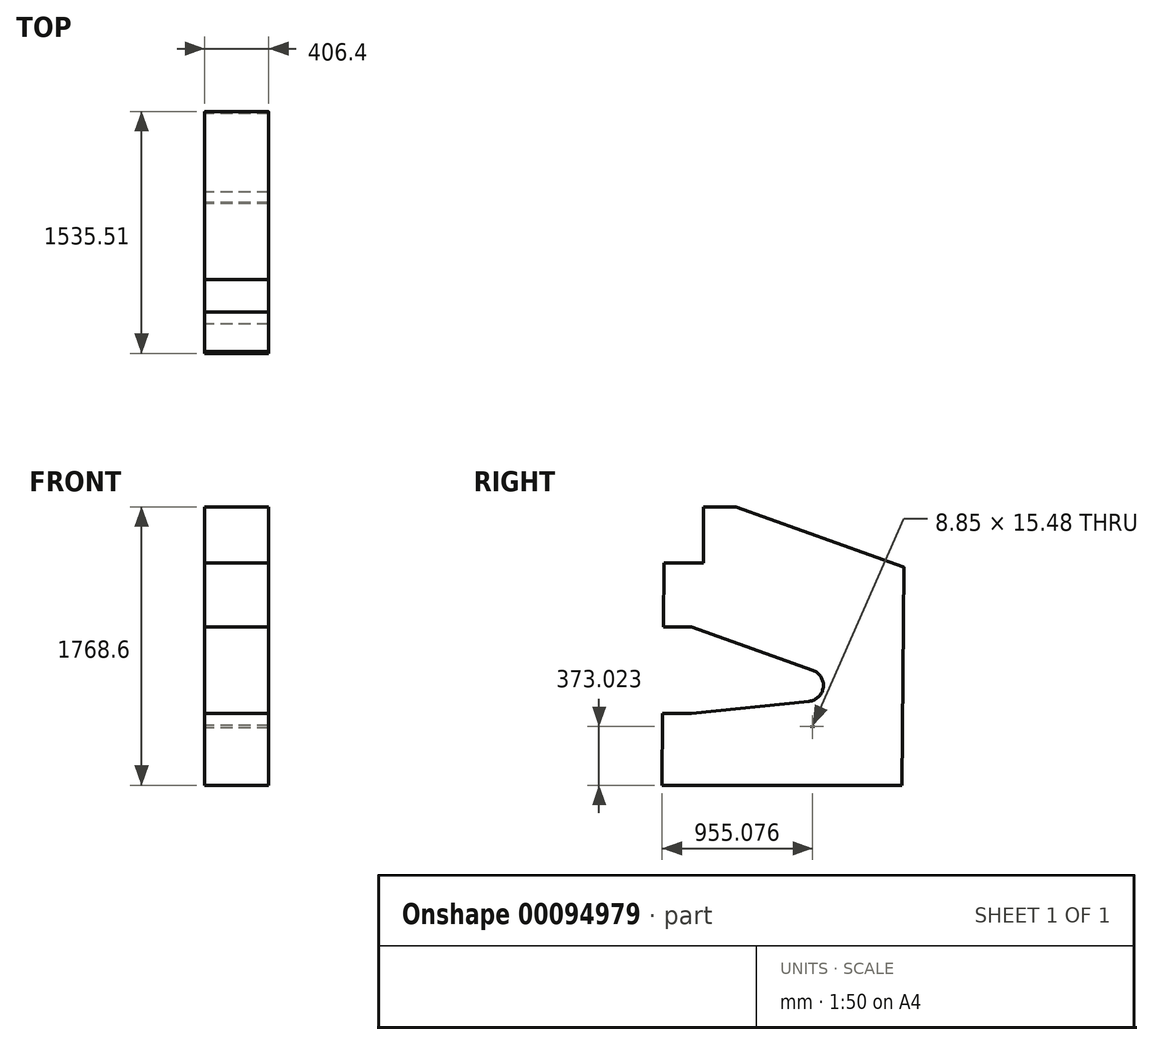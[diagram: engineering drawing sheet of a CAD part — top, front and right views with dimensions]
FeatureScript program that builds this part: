
annotation { "Feature Type Name" : "Feature", "Feature Type Description" : "" }
export const myFeature = defineFeature(function(context is Context, id is Id, definition is map)
    precondition{}
    {
        {
            var Q0;
            Q0=qCreatedBy(makeId("Right.planeOp"),FACE);
            var sketch = newSketch(context, id + "F0", { "sketchPlane" : qUnion([Q0])});
            skLineSegment(sketch, "E0.bottom", {"start": v(601.31, 0) * mm, "end": v(-922.74, 0) * mm});
            skLineSegment(sketch, "E0.top", {"start": v(-736.6, 457.2) * mm, "end": v(-918.95, 457.2) * mm});
            skLineSegment(sketch, "E0.right", {"start": v(-922.74, 0) * mm, "end": v(-918.95, 457.2) * mm});
            skLineSegment(sketch, "E1.bottom", {"start": v(27.91, 365.28) * mm, "end": v(36.76, 365.28) * mm});
            skLineSegment(sketch, "E1.top", {"start": v(27.91, 380.76) * mm, "end": v(36.76, 380.76) * mm});
            skLineSegment(sketch, "E1.left", {"start": v(27.91, 365.28) * mm, "end": v(27.91, 380.76) * mm});
            skLineSegment(sketch, "E1.right", {"start": v(36.76, 365.28) * mm, "end": v(36.76, 380.76) * mm});
            skLineSegment(sketch, "E2.0", {"start": v(-736.6, 1006.6) * mm, "end": v(-914.4, 1006.6) * mm});
            skLineSegment(sketch, "E3.0", {"start": v(-453.6, 1768.6) * mm, "end": v(-660.4, 1768.6) * mm});
            skLineSegment(sketch, "E4.0", {"start": v(0, 635) * mm, "end": v(-914.4, 635) * mm, "construction": true});
            skArc(sketch, "E5", {"start": v(10.38, 533.93) * mm, "mid": v(100.86, 622.77) * mm, "end": v(34.24, 730.66) * mm});
            skLineSegment(sketch, "E6", {"start": v(-736.6, 1221.83) * mm, "end": v(-736.6, 326.78) * mm, "construction": true});
            skLineSegment(sketch, "E7", {"start": v(-736.6, 1006.6) * mm, "end": v(34.24, 730.66) * mm});
            skLineSegment(sketch, "E8", {"start": v(-736.6, 457.2) * mm, "end": v(10.38, 533.93) * mm});
            skLineSegment(sketch, "E9.0", {"start": v(601.31, 0) * mm, "end": v(612.77, 1382.34) * mm});
            skLineSegment(sketch, "E10.0", {"start": v(-453.6, 1768.6) * mm, "end": v(608.56, 1388.37) * mm});
            skLineSegment(sketch, "E11", {"start": v(-911.03, 1413) * mm, "end": v(-660.4, 1413) * mm});
            skLineSegment(sketch, "E12", {"start": v(-660.4, 1413) * mm, "end": v(-660.4, 1768.6) * mm});
            skLineSegment(sketch, "E13", {"start": v(-914.4, 1006.6) * mm, "end": v(-911.03, 1413) * mm});
            skPoint(sketch, "E14.orphan", {"position": v(-909.8, 1413) * mm});
            skPoint(sketch, "E15.orphan", {"position": v(-909.8, 1562.52) * mm});
            skPoint(sketch, "E16.visualSharp", {"position": v(612.8, 1386.85) * mm});
            skArc(sketch, "E16.filletArc", {"start": v(612.77, 1382.34) * mm, "mid": v(611.62, 1386.03) * mm, "end": v(608.56, 1388.37) * mm});
            skSolve(sketch);
        }
        {
            var Q0;
            Q0 = qSketchRegion(id + "F0", true);
            extrude(context, id + "F1", {"entities" : qUnion([Q0]), "endBound" : BoundingType.SYMMETRIC, "depth" : 406.4 * mm});
        }
    });
